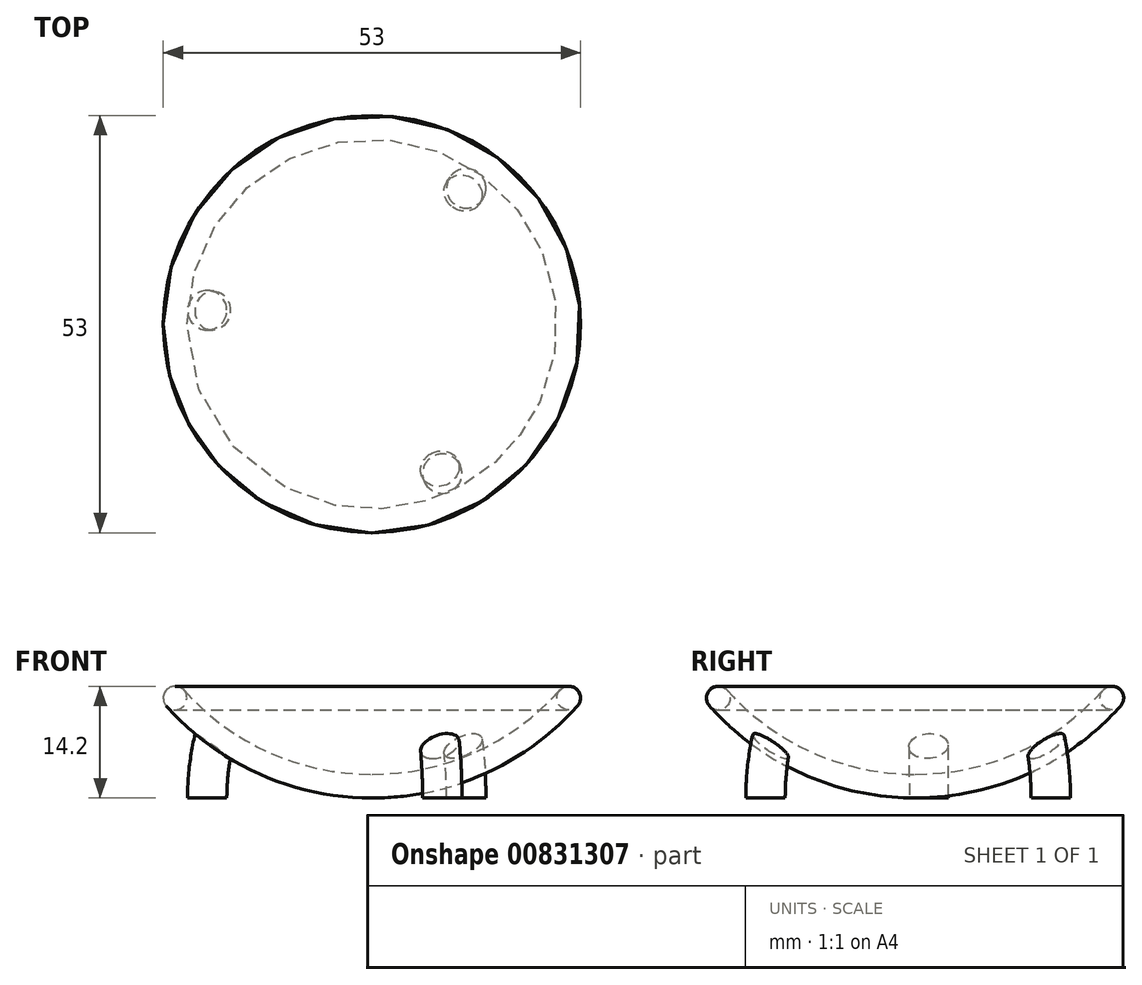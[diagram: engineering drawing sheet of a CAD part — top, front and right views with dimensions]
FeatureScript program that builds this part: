
annotation { "Feature Type Name" : "Feature", "Feature Type Description" : "" }
export const myFeature = defineFeature(function(context is Context, id is Id, definition is map)
    precondition{}
    {
        {
            var Q0;
            Q0=qCreatedBy(makeId("Top.planeOp"),FACE);
            var sketch = newSketch(context, id + "F0", { "sketchPlane" : qUnion([Q0])});
            skPoint(sketch, "E0", {"position": v(30, 0) * mm});
            skCircle(sketch, "E1", {"center": v(30, 0) * mm, "radius": 5 * mm});
            skCircle(sketch, "E2", {"center": v(0, 0) * mm, "radius": 26.5 * mm});
            skCircle(sketch, "E3.cCircle", {"center": v(0, 0) * mm, "radius": 21 * mm, "construction": true});
            skLineSegment(sketch, "E3.0", {"start": v(11.99, 17.24) * mm, "end": v(8.94, -19) * mm});
            skLineSegment(sketch, "E3.1", {"start": v(8.94, -19) * mm, "end": v(-20.93, 1.76) * mm});
            skLineSegment(sketch, "E3.2", {"start": v(-20.93, 1.76) * mm, "end": v(11.99, 17.24) * mm});
            skPoint(sketch, "E4", {"position": v(-20.93, 1.76) * mm});
            skPoint(sketch, "E5", {"position": v(8.94, -19) * mm});
            skPoint(sketch, "E6", {"position": v(11.99, 17.24) * mm});
            skCircle(sketch, "E7", {"center": v(-20.93, 1.76) * mm, "radius": 2.5 * mm});
            skCircle(sketch, "E8", {"center": v(11.99, 17.24) * mm, "radius": 2.5 * mm});
            skCircle(sketch, "E9", {"center": v(8.94, -19) * mm, "radius": 2.5 * mm});
            skSolve(sketch);
        }
        {
            var Q0;
            Q0=qCreatedBy(makeId("Right.planeOp"),FACE);
            var sketch = newSketch(context, id + "F1", { "sketchPlane" : qUnion([Q0])});
            skPoint(sketch, "E10", {"position": v(0, 35) * mm});
            skCircle(sketch, "E11", {"center": v(0, 35) * mm, "radius": 35 * mm});
            skCircle(sketch, "E12", {"center": v(0, 35) * mm, "radius": 33.5 * mm});
            skCircle(sketch, "E13", {"center": v(0, 35) * mm, "radius": 32 * mm});
            skPoint(sketch, "E14", {"position": v(-35, 35) * mm});
            skPoint(sketch, "E15", {"position": v(-33.5, 35) * mm});
            skPoint(sketch, "E16", {"position": v(-32, 35) * mm});
            skPoint(sketch, "E17", {"position": v(0, 1.5) * mm});
            skPoint(sketch, "E18", {"position": v(0, 3) * mm});
            skCircle(sketch, "E19", {"center": v(-25, 12.7) * mm, "radius": 1.5 * mm});
            skCircle(sketch, "E20", {"center": v(25, 12.7) * mm, "radius": 1.5 * mm});
            skLineSegment(sketch, "E21", {"start": v(0, 0) * mm, "end": v(0, 138.6) * mm});
            skSolve(sketch);
        }
        {
            var Q0;
            {var subQ0=sQuery(id+"F1.wireOp",EDGE,"E19");var subQ1=sQuery(id+"F1.wireOp",EDGE,"E12");var subQ2=makeQuery(id+"F1.imprint","INTERSECT",VERTEX,{"disambiguationData":[OD(1.0)],"derivedFrom":[subQ1,subQ0]});Q0=makeQuery(id+"F1.imprint","IMPRINT",FACE,{"disambiguationData":[TD([[makeQuery(id+"F1.imprint","IMPRINT",EDGE,{"disambiguationData":[TD([[subQ2,-1.0]])],"derivedFrom":subQ1}),1.0]])]});}
            var Q1;
            {var subQ0=sQuery(id+"F1.wireOp",EDGE,"E19");var subQ1=sQuery(id+"F1.wireOp",EDGE,"E11");var subQ2=makeQuery(id+"F1.imprint","INTERSECT",VERTEX,{"derivedFrom":[subQ1,subQ0]});Q1=makeQuery(id+"F1.imprint","IMPRINT",FACE,{"disambiguationData":[TD([[makeQuery(id+"F1.imprint","IMPRINT",EDGE,{"disambiguationData":[TD([[subQ2,-1.0]])],"derivedFrom":subQ1}),1.0]])]});}
            var Q2;
            {var subQ0=sQuery(id+"F1.wireOp",EDGE,"E19");var subQ1=sQuery(id+"F1.wireOp",EDGE,"E12");var subQ2=makeQuery(id+"F1.imprint","INTERSECT",VERTEX,{"disambiguationData":[OD(0.0)],"derivedFrom":[subQ1,subQ0]});Q2=makeQuery(id+"F1.imprint","IMPRINT",FACE,{"disambiguationData":[TD([[makeQuery(id+"F1.imprint","IMPRINT",EDGE,{"disambiguationData":[TD([[subQ2,-1.0]])],"derivedFrom":subQ1}),-1.0]])]});}
            var Q3;
            {var subQ0=sQuery(id+"F1.wireOp",EDGE,"E19");var subQ1=sQuery(id+"F1.wireOp",EDGE,"E12");var subQ2=makeQuery(id+"F1.imprint","INTERSECT",VERTEX,{"disambiguationData":[OD(0.0)],"derivedFrom":[subQ1,subQ0]});Q3=makeQuery(id+"F1.imprint","IMPRINT",FACE,{"disambiguationData":[TD([[makeQuery(id+"F1.imprint","IMPRINT",EDGE,{"disambiguationData":[TD([[subQ2,-1.0]])],"derivedFrom":subQ1}),1.0]])]});}
            var Q4;
            {var subQ0=sQuery(id+"F1.wireOp",EDGE,"E20");var subQ1=sQuery(id+"F1.wireOp",EDGE,"E12");var subQ2=makeQuery(id+"F1.imprint","INTERSECT",VERTEX,{"disambiguationData":[OD(0.0)],"derivedFrom":[subQ1,subQ0]});Q4=makeQuery(id+"F1.imprint","IMPRINT",FACE,{"disambiguationData":[TD([[makeQuery(id+"F1.imprint","IMPRINT",EDGE,{"disambiguationData":[TD([[subQ2,-1.0]])],"derivedFrom":subQ1}),-1.0]])]});}
            var Q5;
            {var subQ0=sQuery(id+"F1.wireOp",EDGE,"E20");var subQ1=sQuery(id+"F1.wireOp",EDGE,"E12");var subQ2=makeQuery(id+"F1.imprint","INTERSECT",VERTEX,{"disambiguationData":[OD(0.0)],"derivedFrom":[subQ1,subQ0]});Q5=makeQuery(id+"F1.imprint","IMPRINT",FACE,{"disambiguationData":[TD([[makeQuery(id+"F1.imprint","IMPRINT",EDGE,{"disambiguationData":[TD([[subQ2,-1.0]])],"derivedFrom":subQ1}),1.0]])]});}
            var Q6;
            Q6=sQuery(id+"F1.wireOp",EDGE,"E21");
            revolve(context, id + "F2", {"surfaceOperationType" : NewSurfaceOperationType.NEW, "entities" : qUnion([Q0, Q1, Q2, Q3, Q4, Q5]), "axis" : qUnion([Q6]), "revolveType" : RevolveType.FULL});
        }
        {
            var Q0;
            {var subQ0=sQuery(id+"F0.wireOp",EDGE,"E3.1");var subQ1=sQuery(id+"F0.wireOp",EDGE,"E3.0");var subQ2=makeQuery(id+"F0.imprint","INTERSECT",VERTEX,{"derivedFrom":[subQ1,subQ0]});Q0=makeQuery(id+"F0.imprint","IMPRINT",FACE,{"disambiguationData":[TD([[makeQuery(id+"F0.imprint","IMPRINT",EDGE,{"disambiguationData":[TD([[subQ2,1.0]])],"derivedFrom":subQ1}),1.0]])]});}
            var Q1;
            {var subQ0=sQuery(id+"F0.wireOp",EDGE,"E3.1");var subQ1=sQuery(id+"F0.wireOp",EDGE,"E3.0");var subQ2=makeQuery(id+"F0.imprint","INTERSECT",VERTEX,{"derivedFrom":[subQ1,subQ0]});Q1=makeQuery(id+"F0.imprint","IMPRINT",FACE,{"disambiguationData":[TD([[makeQuery(id+"F0.imprint","IMPRINT",EDGE,{"disambiguationData":[TD([[subQ2,1.0]])],"derivedFrom":subQ1}),-1.0]])]});}
            var Q2;
            Q2=sQuery(id+"F0.wireOp",EDGE,"E3.2");
            revolve(context, id + "F3", {"operationType" : NewBodyOperationType.ADD, "surfaceOperationType" : NewSurfaceOperationType.NEW, "entities" : qUnion([Q0, Q1]), "axis" : qUnion([Q2]), "revolveType" : RevolveType.ONE_DIRECTION, "oppositeDirection" : true, "angle" : 15 * degree});
        }
        {
            var Q0;
            {var subQ0=sQuery(id+"F0.wireOp",EDGE,"E3.2");var subQ1=sQuery(id+"F0.wireOp",EDGE,"E3.0");var subQ2=makeQuery(id+"F0.imprint","INTERSECT",VERTEX,{"derivedFrom":[subQ1,subQ0]});Q0=makeQuery(id+"F0.imprint","IMPRINT",FACE,{"disambiguationData":[TD([[makeQuery(id+"F0.imprint","IMPRINT",EDGE,{"disambiguationData":[TD([[subQ2,-1.0]])],"derivedFrom":subQ1}),-1.0]])]});}
            var Q1;
            {var subQ0=sQuery(id+"F0.wireOp",EDGE,"E3.2");var subQ1=sQuery(id+"F0.wireOp",EDGE,"E3.0");var subQ2=makeQuery(id+"F0.imprint","INTERSECT",VERTEX,{"derivedFrom":[subQ1,subQ0]});Q1=makeQuery(id+"F0.imprint","IMPRINT",FACE,{"disambiguationData":[TD([[makeQuery(id+"F0.imprint","IMPRINT",EDGE,{"disambiguationData":[TD([[subQ2,-1.0]])],"derivedFrom":subQ1}),1.0]])]});}
            var Q2;
            Q2=sQuery(id+"F0.wireOp",EDGE,"E3.1");
            revolve(context, id + "F4", {"operationType" : NewBodyOperationType.ADD, "surfaceOperationType" : NewSurfaceOperationType.NEW, "entities" : qUnion([Q0, Q1]), "axis" : qUnion([Q2]), "revolveType" : RevolveType.ONE_DIRECTION, "oppositeDirection" : true, "angle" : 15 * degree});
        }
        {
            var Q0;
            {var subQ0=sQuery(id+"F0.wireOp",EDGE,"E3.2");var subQ1=sQuery(id+"F0.wireOp",EDGE,"E3.1");var subQ2=makeQuery(id+"F0.imprint","INTERSECT",VERTEX,{"derivedFrom":[subQ1,subQ0]});Q0=makeQuery(id+"F0.imprint","IMPRINT",FACE,{"disambiguationData":[TD([[makeQuery(id+"F0.imprint","IMPRINT",EDGE,{"disambiguationData":[TD([[subQ2,1.0]])],"derivedFrom":subQ1}),-1.0]])]});}
            var Q1;
            {var subQ0=sQuery(id+"F0.wireOp",EDGE,"E3.2");var subQ1=sQuery(id+"F0.wireOp",EDGE,"E3.1");var subQ2=makeQuery(id+"F0.imprint","INTERSECT",VERTEX,{"derivedFrom":[subQ1,subQ0]});Q1=makeQuery(id+"F0.imprint","IMPRINT",FACE,{"disambiguationData":[TD([[makeQuery(id+"F0.imprint","IMPRINT",EDGE,{"disambiguationData":[TD([[subQ2,1.0]])],"derivedFrom":subQ1}),1.0]])]});}
            var Q2;
            Q2=sQuery(id+"F0.wireOp",EDGE,"E3.0");
            revolve(context, id + "F5", {"operationType" : NewBodyOperationType.ADD, "surfaceOperationType" : NewSurfaceOperationType.NEW, "entities" : qUnion([Q0, Q1]), "axis" : qUnion([Q2]), "revolveType" : RevolveType.ONE_DIRECTION, "oppositeDirection" : true, "angle" : 15 * degree});
        }
    });
